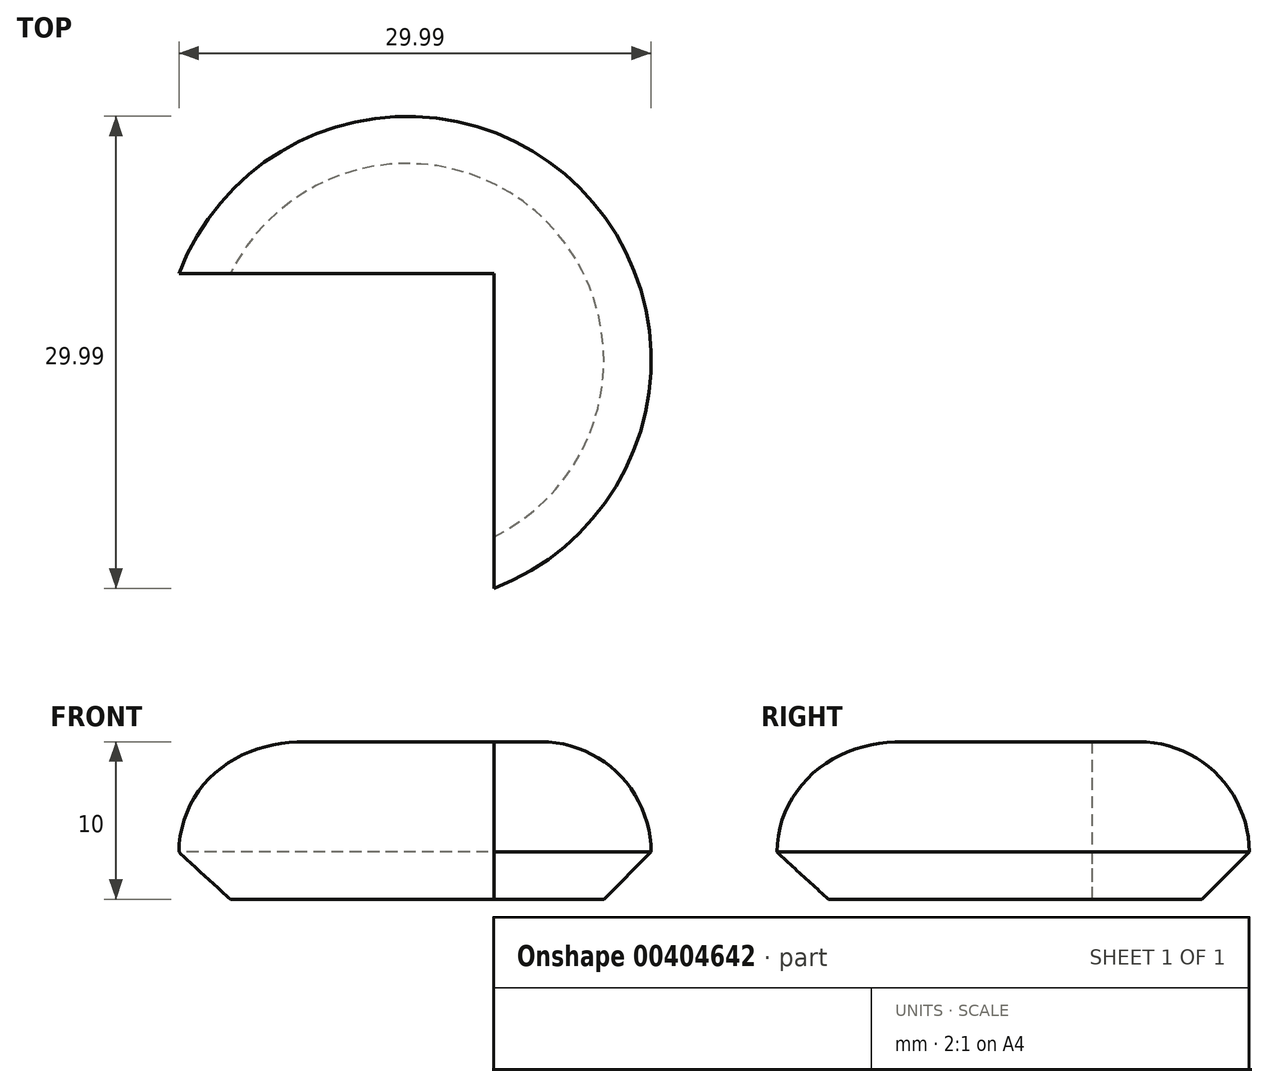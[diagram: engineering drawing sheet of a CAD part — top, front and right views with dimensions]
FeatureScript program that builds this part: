
annotation { "Feature Type Name" : "Feature", "Feature Type Description" : "" }
export const myFeature = defineFeature(function(context is Context, id is Id, definition is map)
    precondition{}
    {
        {
            var Q0;
            Q0=qCreatedBy(makeId("Top.planeOp"),FACE);
            var sketch = newSketch(context, id + "F0", { "sketchPlane" : qUnion([Q0])});
            skLineSegment(sketch, "E0", {"start": v(0, 0) * mm, "end": v(-20, 0) * mm});
            skLineSegment(sketch, "E1", {"start": v(0, 0) * mm, "end": v(0, -20) * mm});
            skArc(sketch, "E2", {"start": v(0, -20) * mm, "mid": v(5.45, 5.45) * mm, "end": v(-20, 0) * mm});
            skSolve(sketch);
        }
        {
            var Q0;
            Q0 = qSketchRegion(id + "F0", true);
            extrude(context, id + "F1", {"entities" : qUnion([Q0]), "depth" : 10 * mm, "offsetDistance" : 25 * mm});
        }
        {
            var Q0;
            Q0=makeQuery(id+"F1.opExtrude","CAP_EDGE",EDGE,{"disambiguationData":[OSD([sQuery(id+"F0.wireOp",EDGE,"E2")])],"isStart":false});
            fillet(context, id + "F2", {"entities" : qUnion([Q0]), "tangentPropagation" : true, "radius" : 7 * mm, "defaultsChanged" : true, "vertexSettings" : [], "allowEdgeOverflow" : false});
        }
        {
            var Q0;
            Q0=makeQuery(id+"F1.opExtrude","CAP_EDGE",EDGE,{"disambiguationData":[OSD([sQuery(id+"F0.wireOp",EDGE,"E2")])],"isStart":true});
            chamfer(context, id + "F3", {"entities" : qUnion([Q0]), "width" : 3 * mm, "tangentPropagation" : true});
        }
    });
